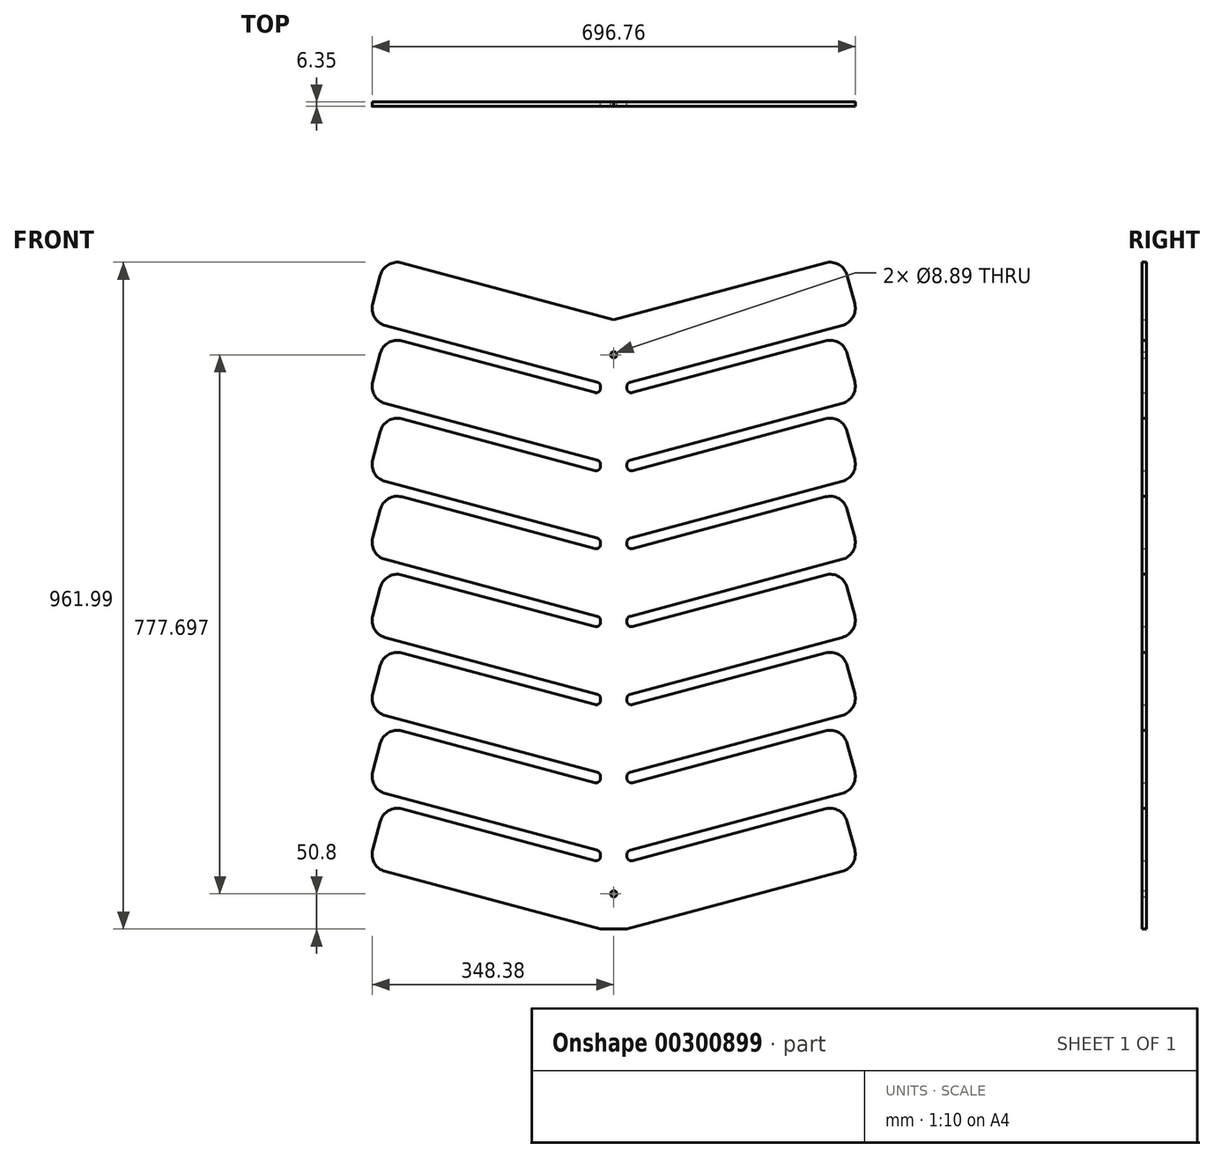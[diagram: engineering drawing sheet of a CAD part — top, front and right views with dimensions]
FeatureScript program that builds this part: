
annotation { "Feature Type Name" : "Feature", "Feature Type Description" : "" }
export const myFeature = defineFeature(function(context is Context, id is Id, definition is map)
    precondition{}
    {
        {
            var Q0;
            Q0=qCreatedBy(makeId("Front.planeOp"),FACE);
            var sketch = newSketch(context, id + "F0", { "sketchPlane" : qUnion([Q0])});
            skLineSegment(sketch, "E0", {"start": v(0, 0) * mm, "end": v(19.05, 0) * mm});
            skLineSegment(sketch, "E1", {"start": v(19.05, 0) * mm, "end": v(329.55, 83.2) * mm});
            skLineSegment(sketch, "E2", {"start": v(305.4, 173.38) * mm, "end": v(27.04, 98.8) * mm});
            skLineSegment(sketch, "E3", {"start": v(19.05, 104.93) * mm, "end": v(19.05, 107.66) * mm});
            skLineSegment(sketch, "E4", {"start": v(347.52, 114.3) * mm, "end": v(336.5, 155.42) * mm});
            skPoint(sketch, "E5.visualSharp", {"position": v(329.92, 179.96) * mm});
            skArc(sketch, "E5.filletArc", {"start": v(336.5, 155.42) * mm, "mid": v(324.66, 170.85) * mm, "end": v(305.4, 173.38) * mm});
            skPoint(sketch, "E6.visualSharp", {"position": v(354.09, 89.77) * mm});
            skArc(sketch, "E6.filletArc", {"start": v(329.55, 83.2) * mm, "mid": v(344.98, 95.03) * mm, "end": v(347.52, 114.3) * mm});
            skArc(sketch, "E7.0.1.0", {"start": v(329.55, 195.73) * mm, "mid": v(344.98, 207.57) * mm, "end": v(347.52, 226.84) * mm});
            skLineSegment(sketch, "E7.0.1.1", {"start": v(347.52, 226.84) * mm, "end": v(336.5, 267.96) * mm});
            skPoint(sketch, "E7.0.1.2", {"position": v(354.09, 202.3) * mm});
            skLineSegment(sketch, "E7.0.1.3", {"start": v(305.4, 285.92) * mm, "end": v(27.04, 211.34) * mm});
            skArc(sketch, "E7.0.1.4", {"start": v(336.5, 267.96) * mm, "mid": v(324.66, 283.38) * mm, "end": v(305.4, 285.92) * mm});
            skPoint(sketch, "E7.0.1.5", {"position": v(329.92, 292.5) * mm});
            skLineSegment(sketch, "E7.0.1.6", {"start": v(23.76, 113.8) * mm, "end": v(329.55, 195.73) * mm});
            skLineSegment(sketch, "E7.0.1.7", {"start": v(19.05, 209.2) * mm, "end": v(19.05, 225.07) * mm});
            skArc(sketch, "E7.0.2.0", {"start": v(329.55, 308.27) * mm, "mid": v(344.98, 320.1) * mm, "end": v(347.52, 339.38) * mm});
            skLineSegment(sketch, "E7.0.2.1", {"start": v(347.52, 339.38) * mm, "end": v(336.5, 380.5) * mm});
            skPoint(sketch, "E7.0.2.2", {"position": v(354.09, 314.84) * mm});
            skLineSegment(sketch, "E7.0.2.3", {"start": v(305.4, 398.45) * mm, "end": v(27.04, 323.87) * mm});
            skArc(sketch, "E7.0.2.4", {"start": v(336.5, 380.5) * mm, "mid": v(324.66, 395.92) * mm, "end": v(305.4, 398.45) * mm});
            skPoint(sketch, "E7.0.2.5", {"position": v(329.92, 405.03) * mm});
            skLineSegment(sketch, "E7.0.2.6", {"start": v(23.76, 226.33) * mm, "end": v(329.55, 308.27) * mm});
            skLineSegment(sketch, "E7.0.2.7", {"start": v(19.05, 330) * mm, "end": v(19.05, 332.73) * mm});
            skArc(sketch, "E7.0.3.0", {"start": v(329.55, 420.8) * mm, "mid": v(344.98, 432.64) * mm, "end": v(347.52, 451.91) * mm});
            skLineSegment(sketch, "E7.0.3.1", {"start": v(347.52, 451.91) * mm, "end": v(336.5, 493.03) * mm});
            skPoint(sketch, "E7.0.3.2", {"position": v(354.09, 427.38) * mm});
            skLineSegment(sketch, "E7.0.3.3", {"start": v(305.4, 510.99) * mm, "end": v(27.04, 436.4) * mm});
            skArc(sketch, "E7.0.3.4", {"start": v(336.5, 493.03) * mm, "mid": v(324.66, 508.45) * mm, "end": v(305.4, 510.99) * mm});
            skPoint(sketch, "E7.0.3.5", {"position": v(329.92, 517.56) * mm});
            skLineSegment(sketch, "E7.0.3.6", {"start": v(23.76, 338.87) * mm, "end": v(329.55, 420.8) * mm});
            skLineSegment(sketch, "E7.0.3.7", {"start": v(19.05, 442.54) * mm, "end": v(19.05, 445.27) * mm});
            skArc(sketch, "E7.0.4.0", {"start": v(329.55, 533.34) * mm, "mid": v(344.98, 545.17) * mm, "end": v(347.52, 564.45) * mm});
            skLineSegment(sketch, "E7.0.4.1", {"start": v(347.52, 564.45) * mm, "end": v(336.5, 605.56) * mm});
            skPoint(sketch, "E7.0.4.2", {"position": v(354.09, 539.91) * mm});
            skLineSegment(sketch, "E7.0.4.3", {"start": v(305.4, 623.52) * mm, "end": v(27.04, 548.94) * mm});
            skArc(sketch, "E7.0.4.4", {"start": v(336.5, 605.56) * mm, "mid": v(324.66, 620.98) * mm, "end": v(305.4, 623.52) * mm});
            skPoint(sketch, "E7.0.4.5", {"position": v(329.92, 630.1) * mm});
            skLineSegment(sketch, "E7.0.4.6", {"start": v(23.76, 451.4) * mm, "end": v(329.55, 533.34) * mm});
            skLineSegment(sketch, "E7.0.4.7", {"start": v(19.05, 555.07) * mm, "end": v(19.05, 557.8) * mm});
            skArc(sketch, "E7.0.5.0", {"start": v(329.55, 645.87) * mm, "mid": v(344.98, 657.7) * mm, "end": v(347.52, 676.98) * mm});
            skLineSegment(sketch, "E7.0.5.1", {"start": v(347.52, 676.98) * mm, "end": v(336.5, 718.1) * mm});
            skPoint(sketch, "E7.0.5.2", {"position": v(354.09, 652.45) * mm});
            skLineSegment(sketch, "E7.0.5.3", {"start": v(305.4, 736.06) * mm, "end": v(27.04, 661.47) * mm});
            skArc(sketch, "E7.0.5.4", {"start": v(336.5, 718.1) * mm, "mid": v(324.66, 733.52) * mm, "end": v(305.4, 736.06) * mm});
            skPoint(sketch, "E7.0.5.5", {"position": v(329.92, 742.63) * mm});
            skLineSegment(sketch, "E7.0.5.6", {"start": v(23.76, 563.93) * mm, "end": v(329.55, 645.87) * mm});
            skLineSegment(sketch, "E7.0.5.7", {"start": v(19.05, 667.6) * mm, "end": v(19.05, 670.34) * mm});
            skArc(sketch, "E7.0.6.0", {"start": v(329.55, 758.4) * mm, "mid": v(344.98, 770.24) * mm, "end": v(347.52, 789.52) * mm});
            skLineSegment(sketch, "E7.0.6.1", {"start": v(347.52, 789.52) * mm, "end": v(336.5, 830.63) * mm});
            skPoint(sketch, "E7.0.6.2", {"position": v(354.09, 764.98) * mm});
            skLineSegment(sketch, "E7.0.6.3", {"start": v(305.4, 848.6) * mm, "end": v(27.04, 774) * mm});
            skArc(sketch, "E7.0.6.4", {"start": v(336.5, 830.63) * mm, "mid": v(324.66, 846.05) * mm, "end": v(305.4, 848.6) * mm});
            skPoint(sketch, "E7.0.6.5", {"position": v(329.92, 855.17) * mm});
            skLineSegment(sketch, "E7.0.6.6", {"start": v(23.76, 676.47) * mm, "end": v(329.55, 758.4) * mm});
            skLineSegment(sketch, "E7.0.6.7", {"start": v(19.05, 780.14) * mm, "end": v(19.05, 782.87) * mm});
            skArc(sketch, "E7.0.7.0", {"start": v(329.55, 870.94) * mm, "mid": v(344.98, 882.78) * mm, "end": v(347.52, 902.05) * mm});
            skLineSegment(sketch, "E7.0.7.1", {"start": v(347.52, 902.05) * mm, "end": v(336.5, 943.17) * mm});
            skPoint(sketch, "E7.0.7.2", {"position": v(354.09, 877.52) * mm});
            skLineSegment(sketch, "E7.0.7.3", {"start": v(305.4, 961.13) * mm, "end": v(0, 879.3) * mm});
            skArc(sketch, "E7.0.7.4", {"start": v(336.5, 943.17) * mm, "mid": v(324.66, 958.59) * mm, "end": v(305.4, 961.13) * mm});
            skPoint(sketch, "E7.0.7.5", {"position": v(329.92, 967.7) * mm});
            skLineSegment(sketch, "E7.0.7.6", {"start": v(23.76, 789) * mm, "end": v(329.55, 870.94) * mm});
            skLineSegment(sketch, "E7.direction2", {"start": v(19.05, 217.47) * mm, "end": v(19.05, 220.2) * mm, "construction": true});
            skPoint(sketch, "E8.visualSharp", {"position": v(19.05, 321.73) * mm});
            skArc(sketch, "E8.filletArc", {"start": v(19.05, 330) * mm, "mid": v(21.53, 324.97) * mm, "end": v(27.04, 323.87) * mm});
            skPoint(sketch, "E9.newPointA", {"position": v(19.05, 337.6) * mm});
            skPoint(sketch, "E9.newPointB", {"position": v(19.05, 337.6) * mm});
            skArc(sketch, "E9.filletArc", {"start": v(23.76, 338.87) * mm, "mid": v(20.36, 336.6) * mm, "end": v(19.05, 332.73) * mm});
            skPoint(sketch, "E10.visualSharp", {"position": v(19.05, 96.66) * mm});
            skArc(sketch, "E10.filletArc", {"start": v(19.05, 104.93) * mm, "mid": v(21.53, 99.9) * mm, "end": v(27.04, 98.8) * mm});
            skPoint(sketch, "E11.newPointA", {"position": v(19.05, 112.53) * mm});
            skPoint(sketch, "E11.newPointB", {"position": v(19.05, 112.53) * mm});
            skArc(sketch, "E11.filletArc", {"start": v(23.76, 113.8) * mm, "mid": v(20.36, 111.53) * mm, "end": v(19.05, 107.66) * mm});
            skPoint(sketch, "E12.newPointB", {"position": v(19.05, 209.2) * mm});
            skArc(sketch, "E12.filletArc", {"start": v(19.05, 217.47) * mm, "mid": v(21.53, 212.43) * mm, "end": v(27.04, 211.34) * mm});
            skPoint(sketch, "E13.newPointA", {"position": v(19.05, 225.07) * mm});
            skPoint(sketch, "E13.newPointB", {"position": v(19.05, 225.07) * mm});
            skArc(sketch, "E13.filletArc", {"start": v(23.76, 226.33) * mm, "mid": v(20.36, 224.06) * mm, "end": v(19.05, 220.2) * mm});
            skPoint(sketch, "E14.visualSharp", {"position": v(19.05, 434.26) * mm});
            skArc(sketch, "E14.filletArc", {"start": v(19.05, 442.54) * mm, "mid": v(21.53, 437.5) * mm, "end": v(27.04, 436.4) * mm});
            skPoint(sketch, "E15.newPointA", {"position": v(19.05, 450.14) * mm});
            skPoint(sketch, "E15.newPointB", {"position": v(19.05, 450.14) * mm});
            skArc(sketch, "E15.filletArc", {"start": v(23.76, 451.4) * mm, "mid": v(20.36, 449.13) * mm, "end": v(19.05, 445.27) * mm});
            skPoint(sketch, "E16.visualSharp", {"position": v(19.05, 546.8) * mm});
            skArc(sketch, "E16.filletArc", {"start": v(19.05, 555.07) * mm, "mid": v(21.53, 550.04) * mm, "end": v(27.04, 548.94) * mm});
            skPoint(sketch, "E17.newPointA", {"position": v(19.05, 562.67) * mm});
            skPoint(sketch, "E17.newPointB", {"position": v(19.05, 562.67) * mm});
            skArc(sketch, "E17.filletArc", {"start": v(23.76, 563.93) * mm, "mid": v(20.36, 561.67) * mm, "end": v(19.05, 557.8) * mm});
            skPoint(sketch, "E18.visualSharp", {"position": v(19.05, 659.33) * mm});
            skArc(sketch, "E18.filletArc", {"start": v(19.05, 667.6) * mm, "mid": v(21.53, 662.57) * mm, "end": v(27.04, 661.47) * mm});
            skPoint(sketch, "E19.newPointA", {"position": v(19.05, 675.2) * mm});
            skPoint(sketch, "E19.newPointB", {"position": v(19.05, 675.2) * mm});
            skArc(sketch, "E19.filletArc", {"start": v(23.76, 676.47) * mm, "mid": v(20.36, 674.2) * mm, "end": v(19.05, 670.34) * mm});
            skPoint(sketch, "E20.visualSharp", {"position": v(19.05, 771.87) * mm});
            skArc(sketch, "E20.filletArc", {"start": v(19.05, 780.14) * mm, "mid": v(21.53, 775.1) * mm, "end": v(27.04, 774) * mm});
            skPoint(sketch, "E21.newPointA", {"position": v(19.05, 787.74) * mm});
            skPoint(sketch, "E21.newPointB", {"position": v(19.05, 787.74) * mm});
            skArc(sketch, "E21.filletArc", {"start": v(23.76, 789) * mm, "mid": v(20.36, 786.74) * mm, "end": v(19.05, 782.87) * mm});
            skPoint(sketch, "E22.orphan", {"position": v(19.05, 884.4) * mm});
            skArc(sketch, "E23.MirrorCS", {"start": v(-23.76, 451.4) * mm, "mid": v(-20.36, 449.13) * mm, "end": v(-19.05, 445.27) * mm});
            skLineSegment(sketch, "E24.MirrorCS", {"start": v(-19.05, 330) * mm, "end": v(-19.05, 332.73) * mm});
            skArc(sketch, "E25.MirrorCS", {"start": v(-23.76, 113.8) * mm, "mid": v(-20.36, 111.53) * mm, "end": v(-19.05, 107.66) * mm});
            skLineSegment(sketch, "E26.MirrorCS", {"start": v(-19.05, 442.54) * mm, "end": v(-19.05, 445.27) * mm});
            skArc(sketch, "E27.MirrorCS", {"start": v(-19.05, 330) * mm, "mid": v(-21.53, 324.97) * mm, "end": v(-27.04, 323.87) * mm});
            skLineSegment(sketch, "E28.MirrorCS", {"start": v(-19.05, 112.53) * mm, "end": v(-44.45, 112.53) * mm, "construction": true});
            skArc(sketch, "E29.MirrorCS", {"start": v(-19.05, 104.93) * mm, "mid": v(-21.53, 99.9) * mm, "end": v(-27.04, 98.8) * mm});
            skLineSegment(sketch, "E30.MirrorCS", {"start": v(-19.05, 104.93) * mm, "end": v(-19.05, 107.66) * mm});
            skArc(sketch, "E31.MirrorCS", {"start": v(-23.76, 338.87) * mm, "mid": v(-20.36, 336.6) * mm, "end": v(-19.05, 332.73) * mm});
            skLineSegment(sketch, "E32.MirrorCS", {"start": v(-19.05, 217.47) * mm, "end": v(-19.05, 220.2) * mm, "construction": true});
            skArc(sketch, "E33.MirrorCS", {"start": v(-19.05, 442.54) * mm, "mid": v(-21.53, 437.5) * mm, "end": v(-27.04, 436.4) * mm});
            skArc(sketch, "E34.MirrorCS", {"start": v(-23.76, 226.33) * mm, "mid": v(-20.36, 224.06) * mm, "end": v(-19.05, 220.2) * mm});
            skArc(sketch, "E35.MirrorCS", {"start": v(-23.76, 563.93) * mm, "mid": v(-20.36, 561.67) * mm, "end": v(-19.05, 557.8) * mm});
            skLineSegment(sketch, "E36.MirrorCS", {"start": v(-19.05, 555.07) * mm, "end": v(-19.05, 557.8) * mm});
            skLineSegment(sketch, "E37.MirrorCS", {"start": v(-19.05, 209.2) * mm, "end": v(-19.05, 225.07) * mm});
            skArc(sketch, "E38.MirrorCS", {"start": v(-19.05, 555.07) * mm, "mid": v(-21.53, 550.04) * mm, "end": v(-27.04, 548.94) * mm});
            skArc(sketch, "E39.MirrorCS", {"start": v(-19.05, 217.47) * mm, "mid": v(-21.53, 212.43) * mm, "end": v(-27.04, 211.34) * mm});
            skArc(sketch, "E40.MirrorCS", {"start": v(-19.05, 780.14) * mm, "mid": v(-21.53, 775.1) * mm, "end": v(-27.04, 774) * mm});
            skLineSegment(sketch, "E41.MirrorCS", {"start": v(-19.05, 667.6) * mm, "end": v(-19.05, 670.34) * mm});
            skArc(sketch, "E42.MirrorCS", {"start": v(-23.76, 676.47) * mm, "mid": v(-20.36, 674.2) * mm, "end": v(-19.05, 670.34) * mm});
            skArc(sketch, "E43.MirrorCS", {"start": v(-23.76, 789) * mm, "mid": v(-20.36, 786.74) * mm, "end": v(-19.05, 782.87) * mm});
            skLineSegment(sketch, "E44.MirrorCS", {"start": v(-19.05, 780.14) * mm, "end": v(-19.05, 782.87) * mm});
            skArc(sketch, "E45.MirrorCS", {"start": v(-19.05, 667.6) * mm, "mid": v(-21.53, 662.57) * mm, "end": v(-27.04, 661.47) * mm});
            skArc(sketch, "E46.MirrorCS", {"start": v(-336.5, 830.63) * mm, "mid": v(-324.66, 846.05) * mm, "end": v(-305.4, 848.6) * mm});
            skArc(sketch, "E47.MirrorCS", {"start": v(-329.55, 533.34) * mm, "mid": v(-344.98, 545.17) * mm, "end": v(-347.52, 564.45) * mm});
            skArc(sketch, "E48.MirrorCS", {"start": v(-336.5, 718.1) * mm, "mid": v(-324.66, 733.52) * mm, "end": v(-305.4, 736.06) * mm});
            skArc(sketch, "E49.MirrorCS", {"start": v(-336.5, 943.17) * mm, "mid": v(-324.66, 958.59) * mm, "end": v(-305.4, 961.13) * mm});
            skArc(sketch, "E50.MirrorCS", {"start": v(-336.5, 380.5) * mm, "mid": v(-324.66, 395.92) * mm, "end": v(-305.4, 398.45) * mm});
            skArc(sketch, "E51.MirrorCS", {"start": v(-329.55, 308.27) * mm, "mid": v(-344.98, 320.1) * mm, "end": v(-347.52, 339.38) * mm});
            skArc(sketch, "E52.MirrorCS", {"start": v(-329.55, 758.4) * mm, "mid": v(-344.98, 770.24) * mm, "end": v(-347.52, 789.52) * mm});
            skLineSegment(sketch, "E53.MirrorCS", {"start": v(-347.52, 114.3) * mm, "end": v(-336.5, 155.42) * mm});
            skArc(sketch, "E54.MirrorCS", {"start": v(-336.5, 155.42) * mm, "mid": v(-324.66, 170.85) * mm, "end": v(-305.4, 173.38) * mm});
            skArc(sketch, "E55.MirrorCS", {"start": v(-329.55, 195.73) * mm, "mid": v(-344.98, 207.57) * mm, "end": v(-347.52, 226.84) * mm});
            skArc(sketch, "E56.MirrorCS", {"start": v(-336.5, 267.96) * mm, "mid": v(-324.66, 283.38) * mm, "end": v(-305.4, 285.92) * mm});
            skArc(sketch, "E57.MirrorCS", {"start": v(-336.5, 493.03) * mm, "mid": v(-324.66, 508.45) * mm, "end": v(-305.4, 510.99) * mm});
            skArc(sketch, "E58.MirrorCS", {"start": v(-329.55, 420.8) * mm, "mid": v(-344.98, 432.64) * mm, "end": v(-347.52, 451.91) * mm});
            skArc(sketch, "E59.MirrorCS", {"start": v(-336.5, 605.56) * mm, "mid": v(-324.66, 620.98) * mm, "end": v(-305.4, 623.52) * mm});
            skLineSegment(sketch, "E60.MirrorCS", {"start": v(-347.52, 676.98) * mm, "end": v(-336.5, 718.1) * mm});
            skPoint(sketch, "E61.MirrorP", {"position": v(-19.05, 112.53) * mm});
            skLineSegment(sketch, "E62.MirrorCS", {"start": v(-347.52, 451.91) * mm, "end": v(-336.5, 493.03) * mm});
            skArc(sketch, "E63.MirrorCS", {"start": v(-329.55, 870.94) * mm, "mid": v(-344.98, 882.78) * mm, "end": v(-347.52, 902.05) * mm});
            skArc(sketch, "E64.MirrorCS", {"start": v(-329.55, 645.87) * mm, "mid": v(-344.98, 657.7) * mm, "end": v(-347.52, 676.98) * mm});
            skLineSegment(sketch, "E65.MirrorCS", {"start": v(-347.52, 339.38) * mm, "end": v(-336.5, 380.5) * mm});
            skLineSegment(sketch, "E66.MirrorCS", {"start": v(0, 0) * mm, "end": v(-19.05, 0) * mm});
            skPoint(sketch, "E67.MirrorP", {"position": v(-19.05, 337.6) * mm});
            skArc(sketch, "E68.MirrorCS", {"start": v(-329.55, 83.2) * mm, "mid": v(-344.98, 95.03) * mm, "end": v(-347.52, 114.3) * mm});
            skLineSegment(sketch, "E69.MirrorCS", {"start": v(-347.52, 226.84) * mm, "end": v(-336.5, 267.96) * mm});
            skLineSegment(sketch, "E70.MirrorCS", {"start": v(-347.52, 564.45) * mm, "end": v(-336.5, 605.56) * mm});
            skLineSegment(sketch, "E71.MirrorCS", {"start": v(-347.52, 789.52) * mm, "end": v(-336.5, 830.63) * mm});
            skLineSegment(sketch, "E72.MirrorCS", {"start": v(-347.52, 902.05) * mm, "end": v(-336.5, 943.17) * mm});
            skPoint(sketch, "E73.MirrorP", {"position": v(-19.05, 321.73) * mm});
            skPoint(sketch, "E74.MirrorP", {"position": v(-19.05, 787.74) * mm});
            skPoint(sketch, "E75.MirrorP", {"position": v(-19.05, 225.07) * mm});
            skPoint(sketch, "E76.MirrorP", {"position": v(-19.05, 675.2) * mm});
            skPoint(sketch, "E77.MirrorP", {"position": v(-19.05, 562.67) * mm});
            skPoint(sketch, "E78.MirrorP", {"position": v(-19.05, 450.14) * mm});
            skLineSegment(sketch, "E79.MirrorCS", {"start": v(-305.4, 736.06) * mm, "end": v(-27.04, 661.47) * mm});
            skLineSegment(sketch, "E80.MirrorCS", {"start": v(-23.76, 226.33) * mm, "end": v(-329.55, 308.27) * mm});
            skPoint(sketch, "E81.MirrorP", {"position": v(-19.05, 434.26) * mm});
            skPoint(sketch, "E82.MirrorP", {"position": v(-354.09, 539.91) * mm});
            skPoint(sketch, "E83.MirrorP", {"position": v(-329.92, 179.96) * mm});
            skPoint(sketch, "E84.MirrorP", {"position": v(-354.09, 877.52) * mm});
            skLineSegment(sketch, "E85.MirrorCS", {"start": v(-305.4, 510.99) * mm, "end": v(-27.04, 436.4) * mm});
            skLineSegment(sketch, "E86.MirrorCS", {"start": v(-23.76, 676.47) * mm, "end": v(-329.55, 758.4) * mm});
            skPoint(sketch, "E87.MirrorP", {"position": v(-354.09, 427.38) * mm});
            skPoint(sketch, "E88.MirrorP", {"position": v(-19.05, 884.4) * mm});
            skPoint(sketch, "E89.MirrorP", {"position": v(-19.05, 659.33) * mm});
            skPoint(sketch, "E90.MirrorP", {"position": v(-329.92, 517.56) * mm});
            skPoint(sketch, "E91.MirrorP", {"position": v(-329.92, 967.7) * mm});
            skPoint(sketch, "E92.MirrorP", {"position": v(-19.05, 771.87) * mm});
            skPoint(sketch, "E93.MirrorP", {"position": v(-329.92, 292.5) * mm});
            skLineSegment(sketch, "E94.MirrorCS", {"start": v(-23.76, 338.87) * mm, "end": v(-329.55, 420.8) * mm});
            skLineSegment(sketch, "E95.MirrorCS", {"start": v(-305.4, 848.6) * mm, "end": v(-27.04, 774) * mm});
            skLineSegment(sketch, "E96.MirrorCS", {"start": v(-23.76, 451.4) * mm, "end": v(-329.55, 533.34) * mm});
            skLineSegment(sketch, "E97.MirrorCS", {"start": v(-305.4, 961.13) * mm, "end": v(0, 879.3) * mm});
            skLineSegment(sketch, "E98.MirrorCS", {"start": v(-305.4, 623.52) * mm, "end": v(-27.04, 548.94) * mm});
            skLineSegment(sketch, "E99.MirrorCS", {"start": v(-23.76, 789) * mm, "end": v(-329.55, 870.94) * mm});
            skPoint(sketch, "E100.MirrorP", {"position": v(-329.92, 630.1) * mm});
            skPoint(sketch, "E101.MirrorP", {"position": v(-354.09, 89.77) * mm});
            skLineSegment(sketch, "E102.MirrorCS", {"start": v(-19.05, 0) * mm, "end": v(-329.55, 83.2) * mm});
            skPoint(sketch, "E103.MirrorP", {"position": v(-19.05, 209.2) * mm});
            skPoint(sketch, "E104.MirrorP", {"position": v(-329.92, 855.17) * mm});
            skPoint(sketch, "E105.MirrorP", {"position": v(-329.92, 405.03) * mm});
            skLineSegment(sketch, "E106.MirrorCS", {"start": v(-305.4, 173.38) * mm, "end": v(-27.04, 98.8) * mm});
            skLineSegment(sketch, "E107.MirrorCS", {"start": v(-305.4, 398.45) * mm, "end": v(-27.04, 323.87) * mm});
            skLineSegment(sketch, "E108.MirrorCS", {"start": v(-305.4, 285.92) * mm, "end": v(-27.04, 211.34) * mm});
            skPoint(sketch, "E109.MirrorP", {"position": v(-329.92, 742.63) * mm});
            skPoint(sketch, "E110.MirrorP", {"position": v(-19.05, 96.66) * mm});
            skLineSegment(sketch, "E111.MirrorCS", {"start": v(-23.76, 113.8) * mm, "end": v(-329.55, 195.73) * mm});
            skPoint(sketch, "E112.MirrorP", {"position": v(-354.09, 202.3) * mm});
            skPoint(sketch, "E113.MirrorP", {"position": v(-354.09, 652.45) * mm});
            skPoint(sketch, "E114.MirrorP", {"position": v(-19.05, 546.8) * mm});
            skPoint(sketch, "E115.MirrorP", {"position": v(-354.09, 314.84) * mm});
            skPoint(sketch, "E116.MirrorP", {"position": v(-354.09, 764.98) * mm});
            skLineSegment(sketch, "E117.MirrorCS", {"start": v(-23.76, 563.93) * mm, "end": v(-329.55, 645.87) * mm});
            skCircle(sketch, "E118", {"center": v(0, 50.8) * mm, "radius": 4.44 * mm});
            skCircle(sketch, "E119", {"center": v(0, 828.5) * mm, "radius": 4.45 * mm});
            skSolve(sketch);
        }
        {
            var Q0;
            Q0=makeQuery(id+"F0.imprint","IMPRINT",FACE,{"disambiguationData":[TD([[makeQuery(id+"F0.imprint","IMPRINT",EDGE,{"derivedFrom":sQuery(id+"F0.wireOp",EDGE,"E0")}),1.0]])]});
            extrude(context, id + "F1", {"entities" : qUnion([Q0]), "depth" : 6.35 * mm});
        }
    });
